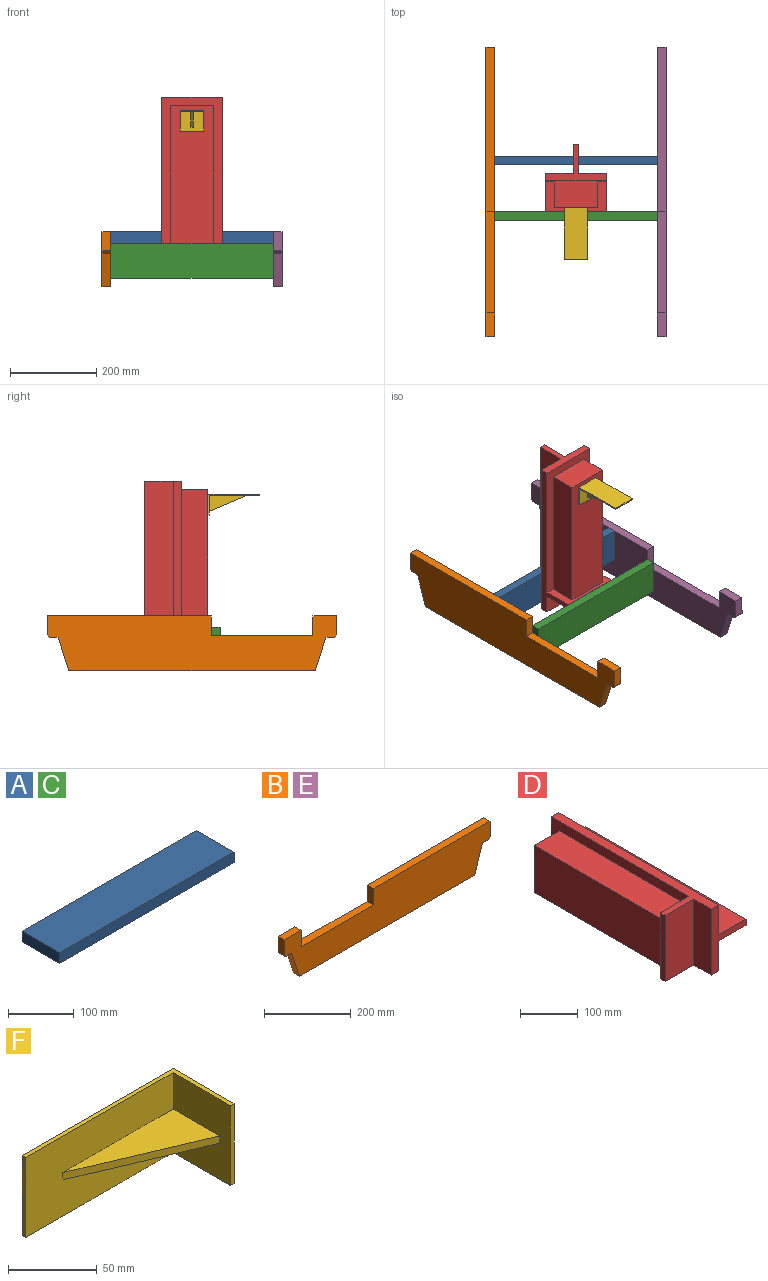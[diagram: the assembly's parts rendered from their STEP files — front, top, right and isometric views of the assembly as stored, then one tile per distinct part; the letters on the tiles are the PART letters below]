
ASSEMBLY  parts=6 mates=4
PART A: 6 faces, bbox 376.7x81x20 mm
  f0: plane 376.7x20mm, normal (0,1,0), area 7534mm2, adj f1,f3,f4,f5
  f1: plane 81x20mm, normal (-1,0,0), area 1620mm2, adj f0,f2,f4,f5
  f2: plane 376.7x20mm, normal (0,-1,0), area 7534mm2, adj f1,f3,f4,f5
  f3: plane 81x20mm, normal (1,0,0), area 1620mm2, adj f0,f2,f4,f5
  f4: plane 376.7x81mm, normal (0,0,1), area 30512.7mm2, adj f0,f1,f2,f3
  f5: plane 376.7x81mm, normal (0,0,-1), area 30512.7mm2, adj f0,f1,f2,f3
PART B: 16 faces, bbox 670x20x127 mm
  f0: plane 55x20mm, normal (0,0,1), area 1100mm2, adj f1,f13,f14,f15
  f1: plane 44x20mm, normal (-1,0,0), area 880mm2, adj f0,f2,f14,f15
  f2: plane 20x5.01mm, normal (-0.71,0,-0.71), area 141.6mm2, adj f1,f3,f14,f15
  f3: plane 20x20mm, normal (0,0,-1), area 400mm2, adj f2,f4,f14,f15
  f4: plane 78x24.99mm, normal (-0.95,0,-0.31), area 1638.1mm2, adj f3,f5,f14,f15
  f5: plane 570x20mm, normal (0,0,-1), area 11400mm2, adj f4,f6,f14,f15
  f6: plane 78x25mm, normal (0.95,0,-0.31), area 1638.1mm2, adj f5,f7,f14,f15
  f7: plane 20x20mm, normal (0,0,-1), area 400mm2, adj f6,f8,f14,f15
  f8: plane 20x5mm, normal (0.71,0,-0.71), area 141.5mm2, adj f7,f9,f14,f15
  f9: plane 44x20mm, normal (1,0,0), area 880mm2, adj f8,f10,f14,f15
  f10: plane 380x20mm, normal (0,0,1), area 7600mm2, adj f9,f11,f14,f15
  f11: plane 46x20mm, normal (-1,0,0), area 920mm2, adj f10,f12,f14,f15
  f12: plane 235x20mm, normal (0,0,1), area 4700mm2, adj f11,f13,f14,f15
  f13: plane 46x20mm, normal (1,0,0), area 920mm2, adj f0,f12,f14,f15
  f14: plane 670x127mm, normal (0,-1,0), area 68404.6mm2, adj f0,f1,f2,f3,f4,f5,f6,f7
  f15: plane 670x127mm, normal (0,1,0), area 68404.6mm2, adj f0,f1,f2,f3,f4,f5,f6,f7
PART C: same geometry as A
PART D: 18 faces, bbox 155x393x140 mm
  f0: plane 338x140mm, normal (-1,0,0), area 15520mm2, adj f1,f3,f12,f13,f15,f16,f17
  f1: plane 140x70mm, normal (0,1,0), area 3617mm2, adj f0,f11,f12,f13,f14,f16,f17
  f2: plane 393x13mm, normal (1,0,0), area 5109mm2, adj f3,f4,f5,f6
  f3: plane 140x85mm, normal (0,1,0), area 3391mm2, adj f0,f2,f5,f6,f7,f10,f12,f13
  f4: plane 140x85mm, normal (0,-1,0), area 3391mm2, adj f2,f5,f6,f7,f9,f10,f12,f13
  f5: plane 393x67mm, normal (0,0,1), area 26331mm2, adj f2,f3,f4,f7
  f6: plane 393x67mm, normal (0,0,-1), area 26331mm2, adj f2,f3,f4,f10
  f7: plane 393x63.5mm, normal (1,0,0), area 24955.5mm2, adj f3,f4,f5,f12
  f8: plane 140x70mm, normal (0,-1,0), area 9800mm2, adj f9,f11,f12,f13
  f9: plane 140x43mm, normal (-1,0,0), area 6020mm2, adj f4,f8,f12,f13
  f10: plane 393x63.5mm, normal (1,0,0), area 24955.5mm2, adj f3,f4,f6,f13
  f11: plane 140x12mm, normal (-1,0,0), area 1680mm2, adj f1,f8,f12,f13
  f12: plane 393x88mm, normal (0,0,1), area 7914mm2, adj f0,f1,f3,f4,f7,f8,f9,f11
  f13: plane 393x88mm, normal (0,0,-1), area 7914mm2, adj f0,f1,f3,f4,f8,f9,f10,f11
  f14: plane 318x100mm, normal (-1,0,0), area 31800mm2, adj f1,f15,f16,f17
  f15: plane 100x61.83mm, normal (0,1,0), area 6183mm2, adj f0,f14,f16,f17
  f16: plane 318x61.83mm, normal (0,0,1), area 19662.1mm2, adj f0,f1,f14,f15
  f17: plane 318x61.83mm, normal (0,0,-1), area 19662.1mm2, adj f0,f1,f14,f15
PART E: same geometry as B
PART F: 11 faces, bbox 120x48.5x55 mm
  f0: plane 117x55mm, normal (0,-1,0), area 5997.6mm2, adj f1,f5,f6,f7,f8,f9,f10
  f1: plane 55x45.46mm, normal (-1,0,0), area 2315.6mm2, adj f0,f2,f6,f7,f8,f9,f10
  f2: plane 55x3mm, normal (0,-1,0), area 165mm2, adj f1,f3,f6,f7
  f3: plane 55x48.46mm, normal (1,0,0), area 2665.5mm2, adj f2,f4,f6,f7
  f4: plane 120x55mm, normal (0,1,0), area 6600mm2, adj f3,f5,f6,f7
  f5: plane 55x3mm, normal (-1,0,0), area 165mm2, adj f0,f4,f6,f7
  f6: plane 120x48.46mm, normal (0,0,1), area 496.4mm2, adj f0,f1,f2,f3,f4,f5
  f7: plane 120x48.46mm, normal (0,0,-1), area 496.4mm2, adj f0,f1,f2,f3,f4,f5
  f8: plane 87.48x36.98mm, normal (-0.39,-0.92,0), area 474.9mm2, adj f0,f1,f9,f10
  f9: plane 87.48x36.98mm, normal (0,0,1), area 1617.4mm2, adj f0,f1,f8
  f10: plane 87.48x36.98mm, normal (0,0,-1), area 1617.4mm2, adj f0,f1,f8
PLACE A rot(axis=(1,0,0),90deg) t=(-573.35,-48,46)mm
PLACE B rot(axis=(0,0,1),90deg) t=(-781.7,-137.11,40.23)mm
PLACE C rot(axis=(1,0,0),90deg) t=(-573.35,-176,20)mm
PLACE D rot(axis=(0.58,0.58,0.58),120deg) t=(-573.35,-125,138.19)mm
PLACE E rot(axis=(0,0,1),90deg) t=(-385,-137.11,40.23)mm
PLACE F rot(axis=(0.58,0.58,0.58),120deg) t=(-573.35,-125,140.81)mm
MATE fastened F.f3 <-> D.f14  axis (0,1,0) through (-573.35,-167.83,368.5)mm
MATE fastened D.f11 <-> C.f5  axis (0,-1,0) through (-573.35,-176,60.5)mm
MATE fastened C.f1 <-> B.f14  axis (-1,0,0) through (-761.7,-186,60.5)mm
MATE fastened A.f1 <-> B.f14  axis (-1,0,0) through (-761.7,-58,86.5)mm
